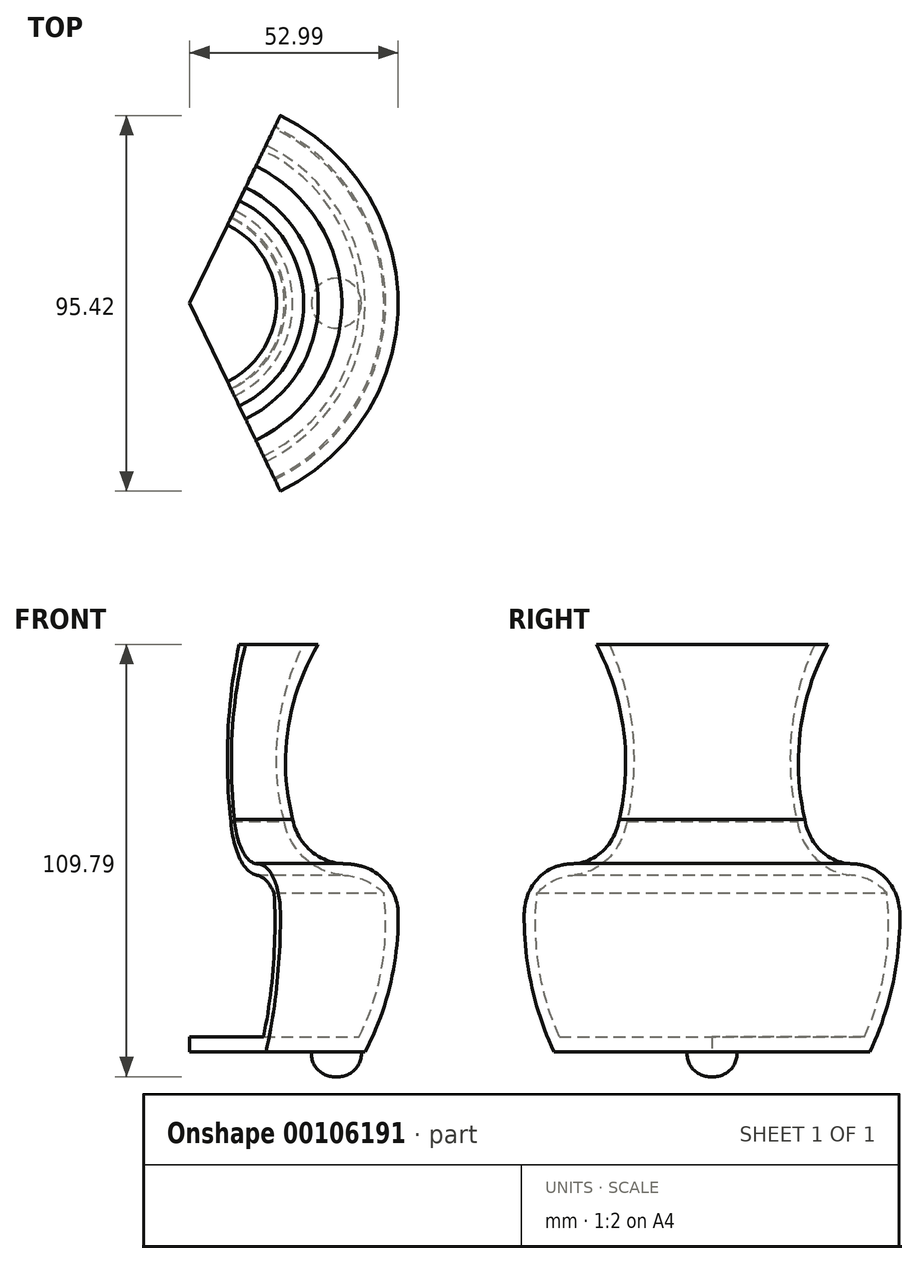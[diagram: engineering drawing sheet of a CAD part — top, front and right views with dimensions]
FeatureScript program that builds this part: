
annotation { "Feature Type Name" : "Feature", "Feature Type Description" : "" }
export const myFeature = defineFeature(function(context is Context, id is Id, definition is map)
    precondition{}
    {
        {
            var Q0;
            Q0=qCreatedBy(makeId("Front.planeOp"),FACE);
            var sketch = newSketch(context, id + "F0", { "sketchPlane" : qUnion([Q0])});
            skLineSegment(sketch, "E0", {"start": v(0, 0) * mm, "end": v(44.6, 0) * mm});
            skArc(sketch, "E1", {"start": v(44.6, 0) * mm, "mid": v(51.6, 19.95) * mm, "end": v(52.67, 41.06) * mm});
            skArc(sketch, "E2", {"start": v(52.67, 41.06) * mm, "mid": v(46.44, 46.06) * mm, "end": v(38.65, 47.77) * mm});
            skArc(sketch, "E3", {"start": v(26.17, 59.04) * mm, "mid": v(30.5, 51.3) * mm, "end": v(38.65, 47.77) * mm});
            skArc(sketch, "E4", {"start": v(32.65, 103.44) * mm, "mid": v(24.97, 81.9) * mm, "end": v(26.17, 59.04) * mm});
            skLineSegment(sketch, "E5", {"start": v(32.65, 103.44) * mm, "end": v(28.97, 103.44) * mm});
            skArc(sketch, "E6", {"start": v(28.97, 103.44) * mm, "mid": v(22.44, 81.39) * mm, "end": v(24.05, 58.44) * mm});
            skArc(sketch, "E7", {"start": v(24.05, 58.44) * mm, "mid": v(29.18, 49.2) * mm, "end": v(38.81, 44.87) * mm});
            skArc(sketch, "E8", {"start": v(49.33, 40.29) * mm, "mid": v(44.5, 43.55) * mm, "end": v(38.81, 44.87) * mm});
            skArc(sketch, "E9", {"start": v(43.06, 3.8) * mm, "mid": v(48.86, 21.59) * mm, "end": v(49.33, 40.29) * mm});
            skLineSegment(sketch, "E10", {"start": v(43.06, 3.8) * mm, "end": v(0, 3.8) * mm});
            skLineSegment(sketch, "E11", {"start": v(0, 3.8) * mm, "end": v(0, 0) * mm});
            skSolve(sketch);
        }
        {
            var Q0;
            Q0=makeQuery(id+"F0.imprint","IMPRINT",FACE,{"disambiguationData":[TD([[makeQuery(id+"F0.imprint","IMPRINT",EDGE,{"derivedFrom":sQuery(id+"F0.wireOp",EDGE,"E0")}),1.0]])]});
            var Q1;
            Q1=sQuery(id+"F0.wireOp",EDGE,"E11");
            revolve(context, id + "F1", {"entities" : qUnion([Q0]), "axis" : qUnion([Q1]), "revolveType" : RevolveType.SYMMETRIC, "angle" : 128.43 * degree});
        }
        {
            var Q0;
            Q0=makeQuery(id+"F1.opRevolve","SWEPT_EDGE",EDGE,{"disambiguationData":[OSD([sQuery(id+"F0.wireOp",EDGE,"E1"),sQuery(id+"F0.wireOp",EDGE,"E2")])]});
            fillet(context, id + "F2", {"entities" : qUnion([Q0]), "radius" : 12.7 * mm, "tangentPropagation" : true, "allowEdgeOverflow" : false});
        }
        {
            var Q0;
            Q0=makeQuery(id+"F1.opRevolve","SWEPT_FACE",FACE,{"disambiguationData":[OSD([sQuery(id+"F0.wireOp",EDGE,"E0")])]});
            var sketch = newSketch(context, id + "F3", { "sketchPlane" : qUnion([Q0])});
            skCircle(sketch, "E12", {"center": v(37.26, 0) * mm, "radius": 6.35 * mm});
            skSolve(sketch);
        }
        {
            var Q0;
            Q0 = qSketchRegion(id + "F3", true);
            extrude(context, id + "F4", {"entities" : qUnion([Q0]), "operationType" : NewBodyOperationType.ADD, "depth" : 6.35 * mm});
        }
        {
            var Q0;
            Q0=makeQuery(id+"F4.opExtrude","CAP_EDGE",EDGE,{"disambiguationData":[OSD([sQuery(id+"F3.wireOp",EDGE,"E12")])],"isStart":false});
            fillet(context, id + "F5", {"entities" : qUnion([Q0]), "radius" : 5.84 * mm, "tangentPropagation" : true, "allowEdgeOverflow" : false});
        }
    });
